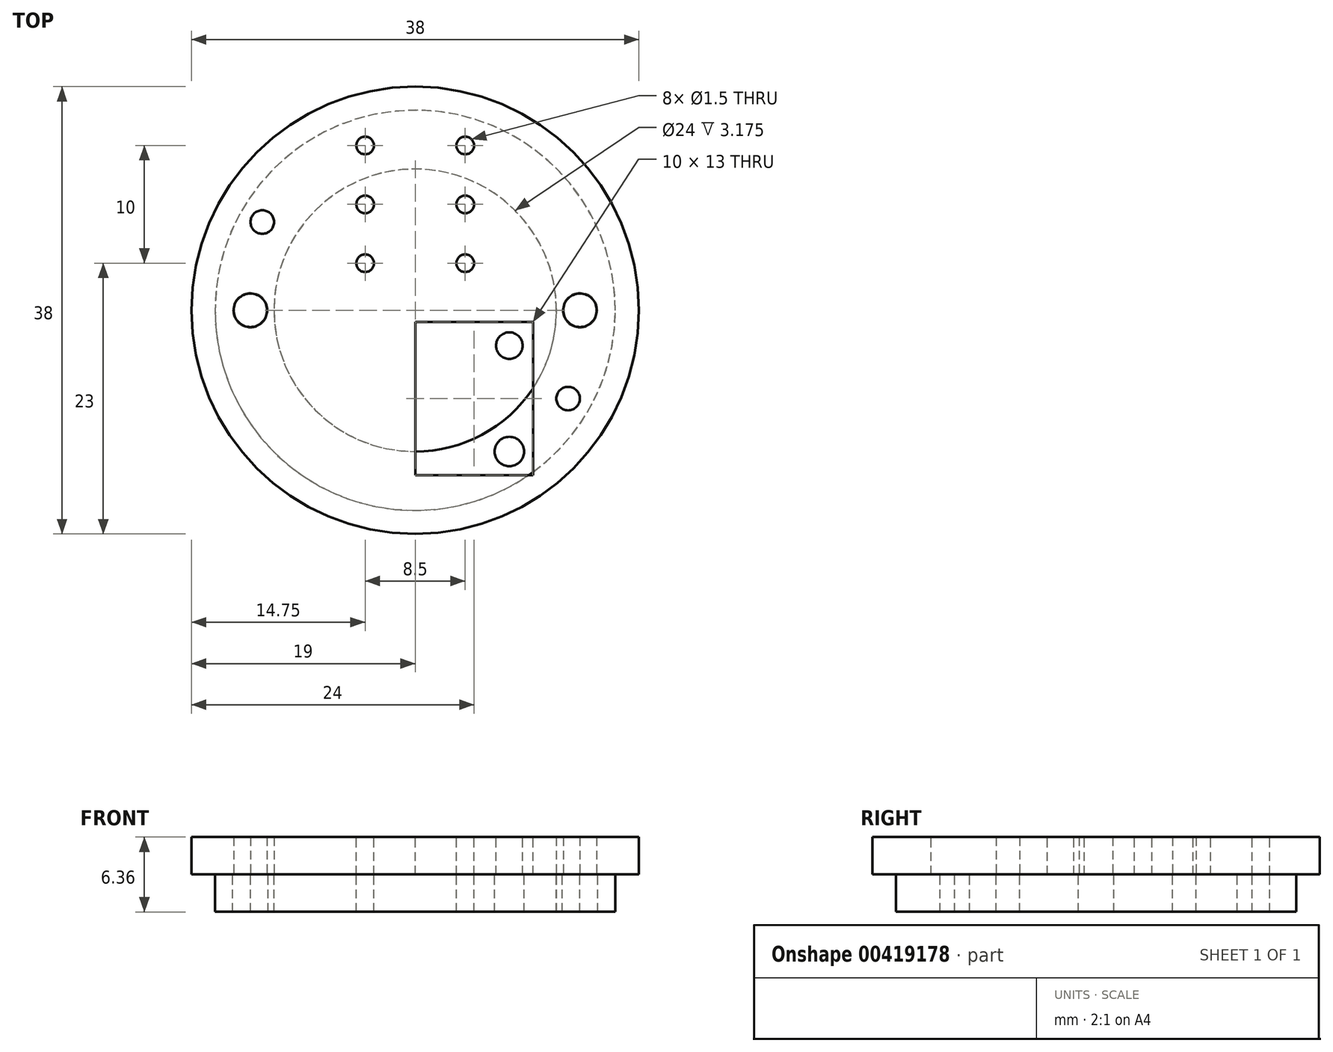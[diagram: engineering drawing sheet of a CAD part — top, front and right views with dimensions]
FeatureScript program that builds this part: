
annotation { "Feature Type Name" : "Feature", "Feature Type Description" : "" }
export const myFeature = defineFeature(function(context is Context, id is Id, definition is map)
    precondition{}
    {
        {
            var Q0;
            Q0=qCreatedBy(makeId("Top.planeOp"),FACE);
            var sketch = newSketch(context, id + "F0", { "sketchPlane" : qUnion([Q0])});
            skCircle(sketch, "E0", {"center": v(0, 0) * mm, "radius": 19 * mm});
            skLineSegment(sketch, "E1", {"start": v(0, 0) * mm, "end": v(14, 0) * mm});
            skCircle(sketch, "E2", {"center": v(14, 0) * mm, "radius": 1.42 * mm});
            skLineSegment(sketch, "E3", {"start": v(0, 0) * mm, "end": v(0, -9.27) * mm});
            skCircle(sketch, "E4.MirrorC", {"center": v(-14, 0) * mm, "radius": 1.42 * mm});
            skLineSegment(sketch, "E5", {"start": v(0, 0) * mm, "end": v(13, -7.5) * mm});
            skCircle(sketch, "E6", {"center": v(13, -7.5) * mm, "radius": 1 * mm});
            skCircle(sketch, "E7.1.0", {"center": v(7.5, 13) * mm, "radius": 1 * mm});
            skCircle(sketch, "E7.2.0", {"center": v(-13, 7.5) * mm, "radius": 1 * mm});
            skCircle(sketch, "E7.3.0", {"center": v(-7.5, -13) * mm, "radius": 1 * mm});
            skSolve(sketch);
        }
        {
            var Q0;
            Q0 = qSketchRegion(id + "F0", true);
            var Q1;
            Q1=makeQuery(id+"F0.imprint","IMPRINT",FACE,{"disambiguationData":[TD([[makeQuery(id+"F0.imprint","IMPRINT",EDGE,{"derivedFrom":sQuery(id+"F0.wireOp",EDGE,"E7.3.0")}),1.0]])]});
            var Q2;
            Q2=makeQuery(id+"F0.imprint","IMPRINT",FACE,{"disambiguationData":[TD([[makeQuery(id+"F0.imprint","IMPRINT",EDGE,{"derivedFrom":sQuery(id+"F0.wireOp",EDGE,"E7.1.0")}),1.0]])]});
            extrude(context, id + "F1", {"entities" : qUnion([Q0, Q1, Q2]), "depth" : 3.17 * mm});
        }
        {
            var Q0;
            Q0=makeQuery(id+"F1.opExtrude","CAP_FACE",FACE,{"disambiguationData":[OSD([sQuery(id+"F0.wireOp",EDGE,"E0"),sQuery(id+"F0.wireOp",EDGE,"E2"),sQuery(id+"F0.wireOp",EDGE,"E4.MirrorC"),sQuery(id+"F0.wireOp",EDGE,"E6"),sQuery(id+"F0.wireOp",EDGE,"E7.1.0"),sQuery(id+"F0.wireOp",EDGE,"E7.2.0"),sQuery(id+"F0.wireOp",EDGE,"E7.3.0")])],"isStart":false});
            var sketch = newSketch(context, id + "F2", { "sketchPlane" : qUnion([Q0])});
            skLineSegment(sketch, "E8", {"start": v(0, 9) * mm, "end": v(0, 14) * mm});
            skLineSegment(sketch, "E9", {"start": v(-4.25, 14) * mm, "end": v(4.25, 14) * mm});
            skLineSegment(sketch, "E10", {"start": v(-4.25, 14) * mm, "end": v(-4.25, 9) * mm});
            skLineSegment(sketch, "E11", {"start": v(-4.25, 9) * mm, "end": v(-4.25, 4) * mm});
            skLineSegment(sketch, "E12", {"start": v(4.25, 14) * mm, "end": v(4.25, 9) * mm});
            skLineSegment(sketch, "E13", {"start": v(4.25, 9) * mm, "end": v(4.25, 4) * mm});
            skCircle(sketch, "E14", {"center": v(4.25, 4) * mm, "radius": 0.75 * mm});
            skCircle(sketch, "E15", {"center": v(4.25, 9) * mm, "radius": 0.75 * mm});
            skCircle(sketch, "E16", {"center": v(4.25, 14) * mm, "radius": 0.75 * mm});
            skCircle(sketch, "E17", {"center": v(-4.25, 14) * mm, "radius": 0.75 * mm});
            skCircle(sketch, "E18", {"center": v(-4.25, 9) * mm, "radius": 0.75 * mm});
            skCircle(sketch, "E19", {"center": v(-4.25, 4) * mm, "radius": 0.75 * mm});
            skLineSegment(sketch, "E20", {"start": v(0, 0) * mm, "end": v(0, 9) * mm});
            skSolve(sketch);
        }
        {
            var Q0;
            Q0 = qSketchRegion(id + "F2", true);
            extrude(context, id + "F3", {"entities" : qUnion([Q0]), "operationType" : NewBodyOperationType.REMOVE, "oppositeDirection" : true, "depth" : 25 * mm});
        }
        {
            var Q0;
            Q0=makeQuery(id+"F1.opExtrude","CAP_FACE",FACE,{"disambiguationData":[OSD([sQuery(id+"F0.wireOp",EDGE,"E0"),sQuery(id+"F0.wireOp",EDGE,"E2"),sQuery(id+"F0.wireOp",EDGE,"E4.MirrorC"),sQuery(id+"F0.wireOp",EDGE,"E6"),sQuery(id+"F0.wireOp",EDGE,"E7.1.0"),sQuery(id+"F0.wireOp",EDGE,"E7.2.0"),sQuery(id+"F0.wireOp",EDGE,"E7.3.0")])],"isStart":false});
            var sketch = newSketch(context, id + "F4", { "sketchPlane" : qUnion([Q0])});
            skLineSegment(sketch, "E21.bottom", {"start": v(-10, -1) * mm, "end": v(10, -1) * mm});
            skLineSegment(sketch, "E21.top", {"start": v(-10, -14) * mm, "end": v(10, -14) * mm});
            skLineSegment(sketch, "E21.left", {"start": v(-10, -1) * mm, "end": v(-10, -14) * mm});
            skLineSegment(sketch, "E21.right", {"start": v(10, -1) * mm, "end": v(10, -14) * mm});
            skLineSegment(sketch, "E22", {"start": v(10, -14) * mm, "end": v(10, -12) * mm});
            skLineSegment(sketch, "E23", {"start": v(10, -12) * mm, "end": v(8, -12) * mm});
            skLineSegment(sketch, "E24", {"start": v(30.12, -7.5) * mm, "end": v(10, -7.5) * mm});
            skCircle(sketch, "E25", {"center": v(8, -12) * mm, "radius": 1.13 * mm});
            skLineSegment(sketch, "E26.MirrorCS", {"start": v(10, -3) * mm, "end": v(8, -3) * mm});
            skCircle(sketch, "E27.MirrorC", {"center": v(8, -3) * mm, "radius": 1.13 * mm});
            skLineSegment(sketch, "E28.MirrorCS", {"start": v(10, -1) * mm, "end": v(10, -3) * mm});
            skLineSegment(sketch, "E29", {"start": v(0, 0) * mm, "end": v(0, -7.5) * mm});
            skLineSegment(sketch, "E30", {"start": v(0, -14) * mm, "end": v(0, -7.5) * mm});
            skSolve(sketch);
        }
        {
            var Q0;
            Q0=makeQuery(id+"F4.imprint","IMPRINT",FACE,{"disambiguationData":[TD([[makeQuery(id+"F4.imprint","IMPRINT",EDGE,{"derivedFrom":sQuery(id+"F4.wireOp",EDGE,"E27.MirrorC")}),-1.0]])]});
            var Q1;
            Q1=makeQuery(id+"F4.imprint","IMPRINT",FACE,{"disambiguationData":[TD([[makeQuery(id+"F4.imprint","IMPRINT",EDGE,{"derivedFrom":sQuery(id+"F4.wireOp",EDGE,"E25")}),1.0]])]});
            extrude(context, id + "F5", {"entities" : qUnion([Q0, Q1]), "operationType" : NewBodyOperationType.REMOVE, "oppositeDirection" : true, "depth" : 25 * mm});
        }
        {
            var Q0;
            Q0=makeQuery(id+"F1.opExtrude","CAP_FACE",FACE,{"disambiguationData":[OSD([sQuery(id+"F0.wireOp",EDGE,"E0"),sQuery(id+"F0.wireOp",EDGE,"E2"),sQuery(id+"F0.wireOp",EDGE,"E4.MirrorC"),sQuery(id+"F0.wireOp",EDGE,"E6"),sQuery(id+"F0.wireOp",EDGE,"E7.2.0")])],"isStart":true});
            var sketch = newSketch(context, id + "F6", { "sketchPlane" : qUnion([Q0])});
            skCircle(sketch, "E31", {"center": v(0, 0) * mm, "radius": 17 * mm});
            skCircle(sketch, "E32", {"center": v(0, 0) * mm, "radius": 12 * mm});
            skCircle(sketch, "E33", {"center": v(-14, 0) * mm, "radius": 1.5 * mm});
            skCircle(sketch, "E34", {"center": v(14, 0) * mm, "radius": 1.5 * mm});
            skCircle(sketch, "E35", {"center": v(13, 7.5) * mm, "radius": 1 * mm});
            skCircle(sketch, "E36", {"center": v(-13, -7.5) * mm, "radius": 1 * mm});
            skCircle(sketch, "E37", {"center": v(-4.25, -14) * mm, "radius": 0.75 * mm});
            skCircle(sketch, "E38", {"center": v(4.25, -14) * mm, "radius": 0.75 * mm});
            skCircle(sketch, "E39", {"center": v(8, 12) * mm, "radius": 1.25 * mm});
            skSolve(sketch);
        }
        {
            var Q0;
            Q0 = qSketchRegion(id + "F6", true);
            extrude(context, id + "F7", {"entities" : qUnion([Q0]), "depth" : 3.17 * mm});
        }
    });
